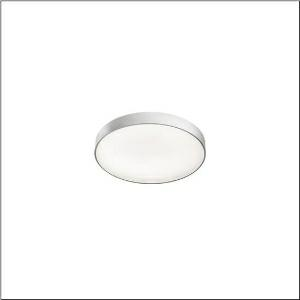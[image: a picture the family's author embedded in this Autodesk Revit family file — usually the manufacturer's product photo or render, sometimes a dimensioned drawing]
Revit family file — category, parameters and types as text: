
# Revit family: round_21_s_51mr34nd0321s
name_source: partatom
category: Lighting Fixtures
units: mm (PartAtom-declared; Revit-internal decimal feet)

## family parameters
Cut with Voids When Loaded = No
Host = Face
Light Source = No
Part Type = Normal
Room Calculation Point = No
Round Connector Dimension = Use Diameter
Shared = No

## types (1)
- Round 21 S (1 x LED, 3660 lm, 28.3 W, 3000K)
    Apparent Load = 28 VA
    CIE Flux Codes = 66 90 98 71 100
    Color Rendering = 80
    Color Temperature = 3000K
    Default Elevation = 1800 mm
    Description = Round 21 S, wall and ceiling luminaire, primary optical cover: micro prismatic cover, of PMMA, transparent, CAT 2 (L<= 3000cd/m²), light emission: direct/indirect distribution, primary light characteristic: symmetric, installation type: suspended mounting, surface-mounted, LED, rated luminous flux: 3.660lm, luminous efficacy: 129lm/W, light colour: 830, colour temperature: 3000K, control gear: DALI 2, with terminal, 5-pole, mains connection: 230V, AC, 50/60Hz, rated input power: 28.3W, housing, of aluminium, coated, silver, diameter: 400mm, height: 62mm, protection rating (complete): IP40, insulation class (complete): insulation class I (protective earthing), certification: CE, impact resistance: IK04, permissible operating ambient temperature: -10..+35°C, packaging unit: 1 piece
    Height = 87 mm
    Lamp = 1 x LED
    Lamp Light Flux = 3660 lm
    Lamp Power = 28.3 W
    Lamp count = 1
    Length = 400 mm
    Luminous efficacy = 129 lm/W
    Manufacturer = Siteco
    ModVariant = No
    Model = 51MR34ND0321S
    Mounting Place = Ceiling
    Mounting Type = Surface mounted
    Number of Poles = 1
    OnlyDefault = Yes
    Power Factor = 1
    Product Name = Round 21 S
    Product group = wall and ceiling luminaire
    ProductGroupID = 304
    Protection Class = Protection class I
    Protection Degree = IP 40
    RLX_Detail_Level = 1
    RLX_Emergency_Light_Flux = 0 lm
    RLX_Emergency_Type = 0
    RLX_Emergency_Type_DB = No
    RlxData = <blob elided: 15145 chars, md5=4b521f5f>
    Socket = socket
    Standby Power = 0 W
    System Light Flux = 3660 lm
    System Power = 28 W
    Type Comments = Product without accessories
    Type Image = l_1258336.jpg
    URL = http://relux.com
    VarID = ---
    Voltage = 0 V
    Weight = 0.00 kg
    Width = 0 mm  [stored 0 ft]

note: [stored X ft] marks values corroborated as IEEE doubles in the binary element streams (Revit-internal decimal feet)

## geometry (parser evidence)
native form markers: Blend x4, Sweep x13
no freeform markers — native parametric forms only
